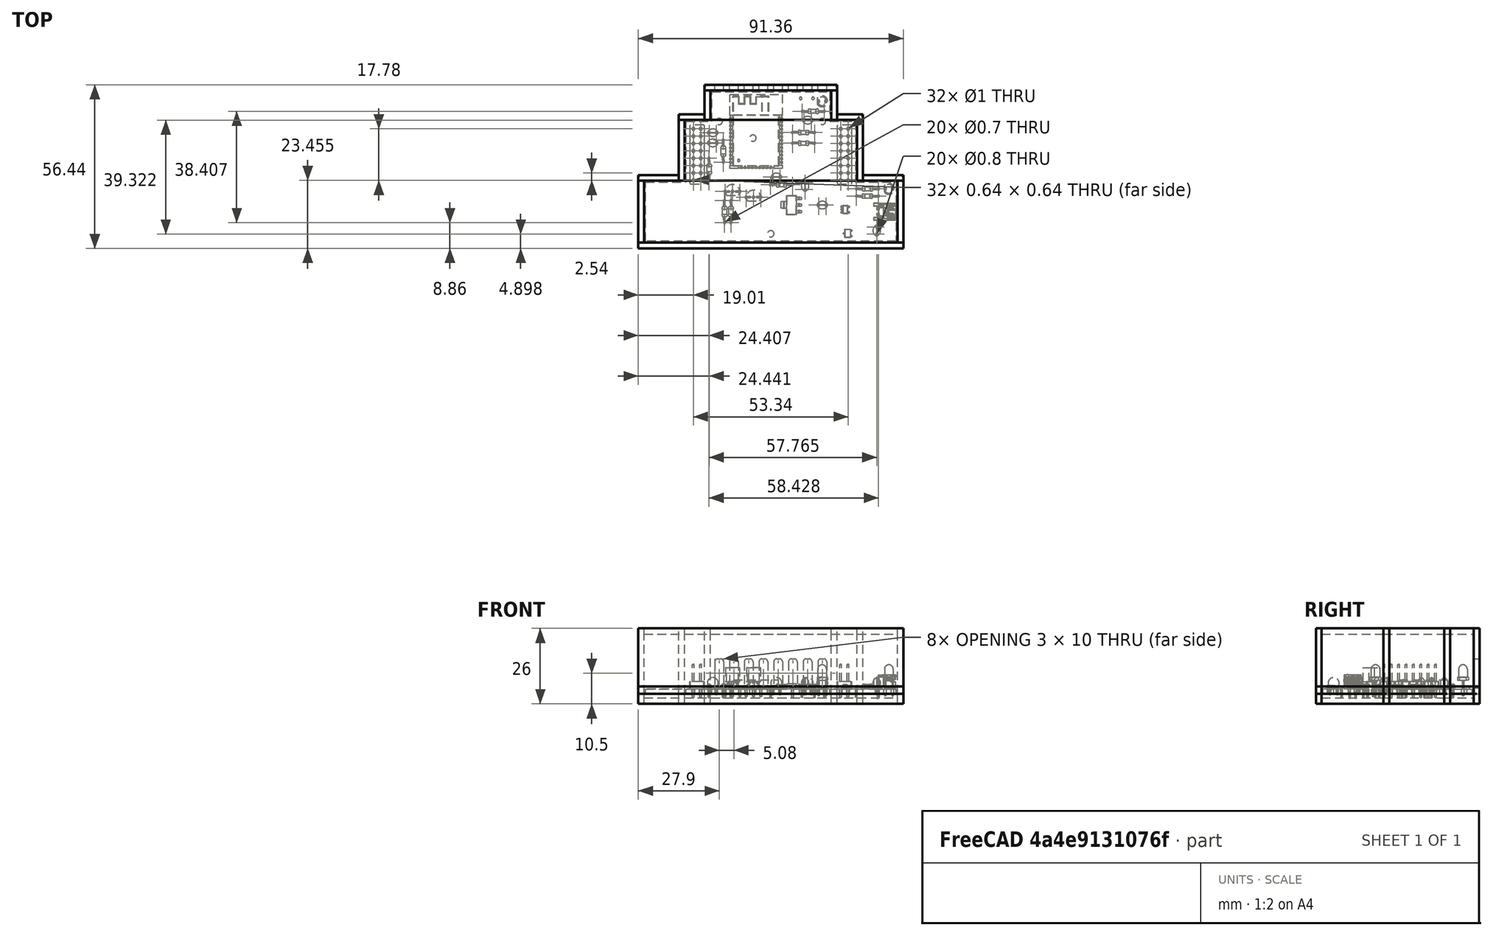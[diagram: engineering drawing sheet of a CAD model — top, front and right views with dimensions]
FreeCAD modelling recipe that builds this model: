
FCSTD DOCUMENT  (FreeCAD 0.16R6704 (Git))
Label: esp32d-diy-box
License: All rights reserved
LicenseURL: http://en.wikipedia.org/wiki/All_rights_reserved
objects: Part::Box×42, Part::Feature×29, Part::Fillet×13, App::DocumentObjectGroup×3, Part::MultiFuse×1, Part::Cut×1
note: 86 computed .brp shape members not serialized (recipe doc carries the construction recipe); baked Part::Feature solids carry a one-line shape summary decoded from their .brp

FEATURE [Part::Box] Box  label="back001"
  Height = 2
  Length = 87.36
  Placement = pos=(-0.5,-0.5,-3.5) rot=(0,0,1;0rad)
  Width = 21.32
FEATURE [Part::Feature] Part__Feature  label="SOLID"
  Placement = pos=(38.1,34.798,1.65) rot=(0,0,1;0rad)
  shape: bbox 18 x 25.5 x 3.1 mm, 751 faces (baked)
FEATURE [Part::Feature] Part__Feature001  label="SOLID001"
  Placement = pos=(67.31,38.735,1.65) rot=(0,0,1;0rad)
  shape: bbox 5.08 x 20.32 x 11.54 mm, 340 faces (baked)
FEATURE [Part::Feature] Part__Feature002  label="SOLID002"
  Placement = pos=(16.51,38.735,1.65) rot=(0,0,1;0rad)
  shape: bbox 5.08 x 20.32 x 11.54 mm, 340 faces (baked)
FEATURE [Part::Feature] Part__Feature003  label="SOLID003"
  Placement = pos=(58.293,33.782,1.65) rot=(0,0,1;3.14159rad)
  shape: bbox 8.285 x 1.732 x 4.666 mm, 17 faces (baked)
FEATURE [Part::Feature] Part__Feature004  label="SOLID004"
  Placement = pos=(58.293,37.465,1.65) rot=(0,0,1;3.14159rad)
  shape: bbox 8.285 x 1.732 x 4.666 mm, 17 faces (baked)
FEATURE [Part::Feature] Part__Feature005  label="SOLID005"
  Placement = pos=(59.5986,48.2143,1.65) rot=(0,0,1;0rad)
  shape: bbox 3.4 x 3.8 x 10.8 mm, 16 faces (baked)
FEATURE [Part::Feature] Part__Feature006  label="SOLID006"
  Placement = pos=(54.0385,44.7675,1.65) rot=(0,0,1;0rad)
  shape: bbox 8.285 x 1.732 x 4.666 mm, 17 faces (baked)
FEATURE [Part::Feature] Part__Feature007  label="SOLID007"
  Placement = pos=(54.6735,41.7195,1.65) rot=(0,0,1;0rad)
  shape: bbox 3.8 x 2.6 x 5.9 mm, 10 faces (baked)
FEATURE [Part::Feature] Part__Feature008  label="SOLID008"
  Placement = pos=(82.6135,18.034,1.65) rot=(0,0,1;0rad)
  shape: bbox 3.4 x 3.8 x 10.8 mm, 16 faces (baked)
FEATURE [Part::Feature] Part__Feature009  label="SOLID009"
  Placement = pos=(72.6897,15.5296,1.65) rot=(0,0,1;0rad)
  shape: bbox 8.285 x 1.732 x 4.666 mm, 17 faces (baked)
FEATURE [Part::Feature] Part__Feature010  label="SOLID010"
  Placement = pos=(50.673,19.431,1.65) rot=(0,0,1;3.14159rad)
  shape: bbox 8.285 x 1.732 x 4.666 mm, 17 faces (baked)
FEATURE [Part::Feature] Part__Feature011  label="SOLID011"
  Placement = pos=(24.4475,37.4015,1.65) rot=(0,0,1;3.14159rad)
  shape: bbox 3.8 x 2.6 x 5.9 mm, 10 faces (baked)
FEATURE [Part::Feature] Part__Feature012  label="SOLID012"
  Placement = pos=(21.9405,33.8633,1.65) rot=(0,0,1;0rad)
  shape: bbox 3.8 x 2.6 x 5.9 mm, 10 faces (baked)
FEATURE [Part::Feature] Part__Feature013  label="SOLID013"
  Placement = pos=(46.3601,22.1336,1.65) rot=(0,0,1;3.14159rad)
  shape: bbox 3.8 x 2.6 x 5.9 mm, 10 faces (baked)
FEATURE [Part::Feature] Part__Feature014  label="SOLID014"
  Placement = pos=(26.797,27.2415,1.65) rot=(0,0,1;1.5708rad)
  shape: bbox 1.732 x 8.285 x 4.666 mm, 17 faces (baked)
FEATURE [Part::Feature] Part__Feature015  label="SOLID015"
  Placement = pos=(21.9075,28.575,1.65) rot=(0,0,-1;1.5708rad)
  shape: bbox 1.732 x 8.285 x 4.666 mm, 17 faces (baked)
FEATURE [Part::Feature] Part__Feature016  label="SOLID016"
  Placement = pos=(27.239,6.36016,1.65) rot=(0,0,1;1.5708rad)
  shape: bbox 1.732 x 8.285 x 4.666 mm, 17 faces (baked)
FEATURE [Part::Feature] Part__Feature017  label="SOLID017"
  Placement = pos=(29.4437,13.9802,1.65) rot=(0,0,-1;1.5708rad)
  shape: bbox 1.732 x 8.285 x 4.666 mm, 17 faces (baked)
FEATURE [Part::Feature] Part__Feature018  label="SOLID018"
  Placement = pos=(27.4574,17.1399,1.65) rot=(0,0,1;0rad)
  shape: bbox 5.58 x 3.745 x 10 mm, 27 faces (baked)
FEATURE [Part::Feature] Part__Feature019  label="SOLID019"
  Placement = pos=(34.6558,15.1587,1.65) rot=(0,0,1;0rad)
  shape: bbox 5.58 x 3.745 x 10 mm, 27 faces (baked)
FEATURE [Part::Feature] Part__Feature020  label="SOLID020"
  Placement = pos=(55.0215,17.7648,1.65) rot=(0,0,1;1.5708rad)
  shape: bbox 2.6 x 3.8 x 5.9 mm, 10 faces (baked)
FEATURE [Part::Feature] Part__Feature021  label="SOLID021"
  Placement = pos=(59.6951,12.4409,1.65) rot=(0,0,1;0rad)
  shape: bbox 3.8 x 2.6 x 5.9 mm, 10 faces (baked)
FEATURE [Part::Feature] Part__Feature022  label="SOLID022"
  Placement = pos=(79.9897,9.16,1.65) rot=(0,0,1;1.5708rad)
  shape: bbox 7.6 x 5.9 x 8.25 mm, 110 faces (baked)
FEATURE [Part::Feature] Part__Feature023  label="SOLID023"
  Placement = pos=(68.8391,10.9322,1.65) rot=(0,0,1;0rad)
  shape: bbox 2.8 x 2.9 x 1.55 mm, 109 faces (baked)
FEATURE [Part::Feature] Part__Feature024  label="SOLID024"
  Placement = pos=(69.6976,2.65684,1.65) rot=(0,0,1;3.14159rad)
  shape: bbox 2.9 x 2.98 x 1.05 mm, 79 faces (baked)
FEATURE [Part::Feature] Part__Feature025  label="SOLID025"
  Placement = pos=(79.7052,2.39776,1.65) rot=(0,0,1;1.5708rad)
  shape: bbox 2.6 x 3.8 x 5.9 mm, 10 faces (baked)
FEATURE [Part::Feature] Part__Feature026  label="SOLID026"
  Placement = pos=(72.7151,18.034,1.65) rot=(0,0,1;0rad)
  shape: bbox 8.285 x 1.732 x 4.666 mm, 17 faces (baked)
FEATURE [Part::Feature] Part__Feature027  label="SOLID027"
  Placement = pos=(50.292,12.446,1.65) rot=(0,0,1;3.14159rad)
  shape: bbox 7 x 6.5 x 1.7 mm, 78 faces (baked)
FEATURE [Part::Feature] Part__Feature028  label="COMPOUND"
  shape: bbox 86.36 x 51.44 x 1.6 mm, 98 faces (baked)
FEATURE [Part::Box] Box001  label="back002"
  Height = 2
  Length = 59.42
  Placement = pos=(13.47,20.82,-3.5) rot=(0,0,1;0rad)
  Width = 20.955
FEATURE [Part::Box] Box002  label="back003"
  Height = 2
  Length = 41.64
  Placement = pos=(22.36,41.775,-3.5) rot=(0,0,1;0rad)
  Width = 10.16
FEATURE [Part::Box] Box003  label="back-left001"
  Height = 6
  Length = 2
  Placement = pos=(-2.5,-0.5,-3.5) rot=(0,0,1;0rad)
  Width = 21.32
FEATURE [Part::Box] Box004  label="back-left002"
  Height = 6
  Length = 2
  Placement = pos=(11.47,20.82,-3.5) rot=(0,0,1;0rad)
  Width = 20.955
FEATURE [Part::Box] Box005  label="back-left003"
  Height = 6
  Length = 2
  Placement = pos=(20.36,41.775,-3.5) rot=(0,0,1;0rad)
  Width = 10.16
FEATURE [Part::Box] Box006  label="back-right001"
  Height = 6
  Length = 2
  Placement = pos=(86.86,-0.5,-3.5) rot=(0,0,1;0rad)
  Width = 21.32
FEATURE [Part::Box] Box007  label="back-right002"
  Height = 6
  Length = 2
  Placement = pos=(72.89,20.82,-3.5) rot=(0,0,1;0rad)
  Width = 20.955
FEATURE [Part::Box] Box008  label="back-right003"
  Height = 6
  Length = 2
  Placement = pos=(64,41.775,-3.5) rot=(0,0,1;0rad)
  Width = 10.16
FEATURE [Part::Box] Box009  label="back-top001"
  Height = 6
  Length = 45.64
  Placement = pos=(20.36,51.935,-3.5) rot=(0,0,1;0rad)
  Width = 2
FEATURE [Part::Box] Box010  label="back-bottom001"
  Height = 6
  Length = 91.36
  Placement = pos=(-2.5,-2.5,-3.5) rot=(0,0,1;0rad)
  Width = 2
FEATURE [Part::Box] Box011  label="back-bottom002"
  Height = 6
  Length = 13.97
  Placement = pos=(-2.5,20.82,-3.5) rot=(0,0,1;0rad)
  Width = 2
FEATURE [Part::Box] Box012  label="back-bottom003"
  Height = 6
  Length = 13.97
  Placement = pos=(74.89,20.82,-3.5) rot=(0,0,1;0rad)
  Width = 2
FEATURE [Part::Box] Box013  label="back-bottom004"
  Height = 6
  Length = 8.89
  Placement = pos=(11.47,41.775,-3.5) rot=(0,0,1;0rad)
  Width = 2
FEATURE [Part::Box] Box014  label="back-bottom005"
  Height = 6
  Length = 8.89
  Placement = pos=(66,41.775,-3.5) rot=(0,0,1;0rad)
  Width = 2
FEATURE [Part::Box] Box015  label="cover-left001"
  Height = 22.5
  Length = 2
  Placement = pos=(-2.5,-0.5,0) rot=(0,0,1;0rad)
  Width = 21.32
FEATURE [Part::Box] Box016  label="cover-left002"
  Height = 22.5
  Length = 2
  Placement = pos=(11.47,20.82,0) rot=(0,0,1;0rad)
  Width = 20.955
FEATURE [Part::Box] Box017  label="cover-left003"
  Height = 22.5
  Length = 2
  Placement = pos=(20.36,41.775,0) rot=(0,0,1;0rad)
  Width = 10.16
FEATURE [Part::Box] Box018  label="cover-right001"
  Height = 22.5
  Length = 2
  Placement = pos=(86.86,-0.5,0) rot=(0,0,1;0rad)
  Width = 21.32
FEATURE [Part::Box] Box019  label="cover-right002"
  Height = 22.5
  Length = 2
  Placement = pos=(72.89,20.82,0) rot=(0,0,1;0rad)
  Width = 20.955
FEATURE [Part::Box] Box020  label="cover-right003"
  Height = 22.5
  Length = 2
  Placement = pos=(64,41.775,0) rot=(0,0,1;0rad)
  Width = 10.16
FEATURE [Part::Box] Box021  label="cover-top001"
  Height = 22.5
  Length = 45.64
  Placement = pos=(20.36,51.935,0) rot=(0,0,1;0rad)
  Width = 2
FEATURE [Part::Box] Box022  label="cover-bottom001"
  Height = 22.5
  Length = 91.36
  Placement = pos=(-2.5,-2.5,0) rot=(0,0,1;0rad)
  Width = 2
FEATURE [Part::Box] Box023  label="cover-bottom002"
  Height = 22.5
  Length = 13.97
  Placement = pos=(-2.5,20.82,0) rot=(0,0,1;0rad)
  Width = 2
FEATURE [Part::Box] Box024  label="cover-bottom003"
  Height = 22.5
  Length = 13.97
  Placement = pos=(74.89,20.82,0) rot=(0,0,1;0rad)
  Width = 2
FEATURE [Part::Box] Box025  label="cover-bottom004"
  Height = 22.5
  Length = 8.89
  Placement = pos=(11.47,41.775,0) rot=(0,0,1;0rad)
  Width = 2
FEATURE [Part::Box] Box026  label="cover-bottom005"
  Height = 22.5
  Length = 8.89
  Placement = pos=(66,41.775,0) rot=(0,0,1;0rad)
  Width = 2
FEATURE [Part::Box] Box027  label="cover001"
  Height = 2
  Length = 87.36
  Placement = pos=(-0.5,-0.5,20.5) rot=(0,0,1;0rad)
  Width = 21.32
FEATURE [Part::Box] Box028  label="cover002"
  Height = 2
  Length = 59.42
  Placement = pos=(13.47,20.82,20.5) rot=(0,0,1;0rad)
  Width = 20.955
FEATURE [Part::Box] Box029  label="cover003"
  Height = 2
  Length = 41.64
  Placement = pos=(22.36,41.775,20.5) rot=(0,0,1;0rad)
  Width = 10.16
FEATURE [Part::Box] Box030  label="back004"
  Height = 2
  Length = 41.64
  Placement = pos=(22.36,41.775,-3.5) rot=(0,0,1;0rad)
  Width = 10.16
FEATURE [App::DocumentObjectGroup] Grup001  label="pcb"
  Group = -> [Part__Feature,Part__Feature001,Part__Feature002,Part__Feature003,Part__Feature004,Part__Feature005,Part__Feature006,Part__Feature007,Part__Feature008,Part__Feature009,Part__Feature010,Part__Feature011,Part__Feature012,Part__Feature013,Part__Feature014,Part__Feature015,Part__Feature016,Part__Feature017,Part__Feature018,Part__Feature019,Part__Feature020,Part__Feature021,Part__Feature022,+6 more]
FEATURE [Part::Box] Box031  label="back005"
  Height = 2
  Length = 41.64
  Placement = pos=(22.36,41.775,-3.5) rot=(0,0,1;0rad)
  Width = 10.16
FEATURE [App::DocumentObjectGroup] Grup  label="back"
  Group = -> [Box030,Box031,Box009,Box010,Box011,Box012,Box013,Box014,Box002,Box003,Box004,Box005,Box006,Box007,Box008,Box001,Box]
FEATURE [Part::Box] Box032  label="cover-hole-top001"
  Height = 10
  Length = 3
  Placement = pos=(59.46,45.775,2) rot=(0,0,1;0rad)
  Width = 10.16
FEATURE [Part::Box] Box033  label="cover-right004"
  Height = 22.5
  Length = 2
  Placement = pos=(64,41.775,0) rot=(0,0,1;0rad)
  Width = 10.16
FEATURE [Part::Box] Box034  label="cover-right005"
  Height = 22.5
  Length = 2
  Placement = pos=(64,41.775,0) rot=(0,0,1;0rad)
  Width = 10.16
FEATURE [Part::Box] Box035  label="cover-hole-top002"
  Height = 10
  Length = 3
  Placement = pos=(54.38,45.775,2) rot=(0,0,1;0rad)
  Width = 10.16
FEATURE [Part::Box] Box036  label="cover-hole-top003"
  Height = 10
  Length = 3
  Placement = pos=(49.3,45.775,2) rot=(0,0,1;0rad)
  Width = 10.16
FEATURE [Part::Box] Box037  label="cover-hole-top004"
  Height = 10
  Length = 3
  Placement = pos=(44.22,45.775,2) rot=(0,0,1;0rad)
  Width = 10.16
FEATURE [Part::Box] Box038  label="cover-hole-top005"
  Height = 10
  Length = 3
  Placement = pos=(39.14,45.775,2) rot=(0,0,1;0rad)
  Width = 10.16
FEATURE [Part::Box] Box039  label="cover-hole-top006"
  Height = 10
  Length = 3
  Placement = pos=(34.06,45.775,2) rot=(0,0,1;0rad)
  Width = 10.16
FEATURE [Part::Box] Box040  label="cover-hole-top007"
  Height = 10
  Length = 3
  Placement = pos=(28.98,45.775,2) rot=(0,0,1;0rad)
  Width = 10.16
FEATURE [Part::Box] Box041  label="cover-hole-top008"
  Height = 10
  Length = 3
  Placement = pos=(23.9,45.775,2) rot=(0,0,1;0rad)
  Width = 10.16
FEATURE [Part::Fillet] Fillet
  Base = -> Box032
  Edges = 4 edges r=1: [Edge2,Edge4,Edge6,Edge8]
FEATURE [Part::Fillet] Fillet001
  Base = -> Box035
  Edges = 4 edges r=1: [Edge2,Edge4,Edge6,Edge8]
FEATURE [Part::Fillet] Fillet002
  Base = -> Box036
  Edges = 4 edges r=1: [Edge2,Edge4,Edge6,Edge8]
FEATURE [Part::Fillet] Fillet003
  Base = -> Box037
  Edges = 4 edges r=1: [Edge2,Edge4,Edge6,Edge8]
FEATURE [Part::Fillet] Fillet004
  Base = -> Box038
  Edges = 4 edges r=1: [Edge2,Edge4,Edge6,Edge8]
FEATURE [Part::Fillet] Fillet005
  Base = -> Box039
  Edges = 4 edges r=1: [Edge2,Edge4,Edge6,Edge8]
FEATURE [Part::Fillet] Fillet006
  Base = -> Box040
  Edges = 4 edges r=1: [Edge2,Edge4,Edge6,Edge8]
FEATURE [Part::Fillet] Fillet007
  Base = -> Box041
  Edges = 4 edges r=1: [Edge2,Edge4,Edge6,Edge8]
FEATURE [Part::MultiFuse] Fusion
  Shapes = -> [Fillet,Fillet002,Fillet001,Fillet003,Fillet004,Fillet005,Fillet006,Fillet007]
FEATURE [Part::Fillet] Fillet008
  Base = -> Box021
  Edges = 2 edges r=1: [Edge3,Edge7]
FEATURE [Part::Cut] Cut
  Base = -> Fillet008
  Tool = -> Fusion
FEATURE [Part::Fillet] Fillet009
  Base = -> Box025
  Edges = 1 edges r=1: [Edge3]
FEATURE [Part::Fillet] Fillet010
  Base = -> Box026
  Edges = 1 edges r=1: [Edge7]
FEATURE [Part::Fillet] Fillet011
  Base = -> Box023
  Edges = 1 edges r=1: [Edge3]
FEATURE [Part::Fillet] Fillet012
  Base = -> Box024
  Edges = 1 edges r=1: [Edge7]
FEATURE [App::DocumentObjectGroup] Grup002  label="cover"
  Group = -> [Box027,Box028,Box029,Box022,Box023,Box024,Box025,Box026,Box015,Box016,Box017,Box018,Box019,Box020,Box033,Box034,Cut,Fillet009,Fillet010,Fillet011,Fillet012]
